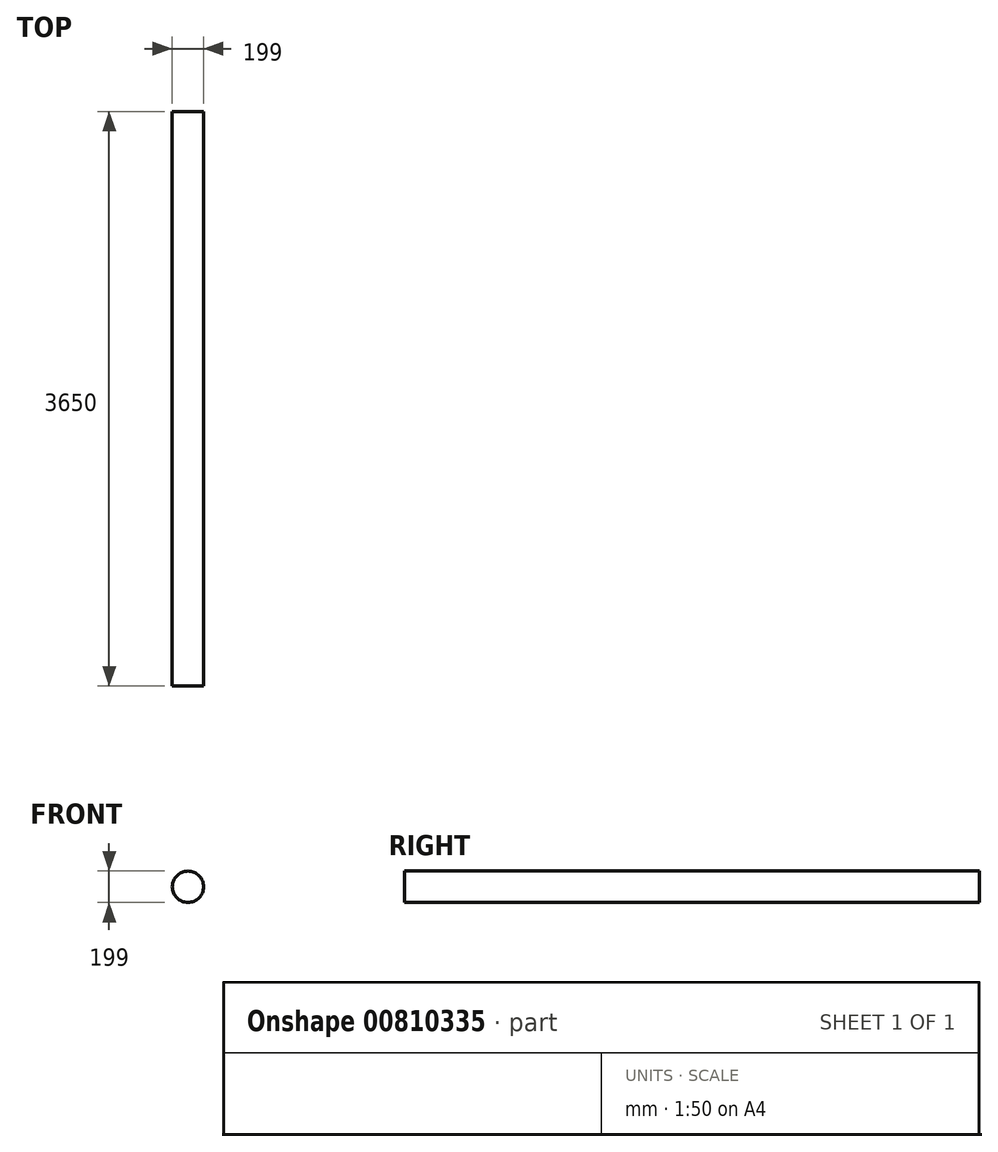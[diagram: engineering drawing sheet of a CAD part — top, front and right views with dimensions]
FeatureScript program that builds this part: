
annotation { "Feature Type Name" : "Feature", "Feature Type Description" : "" }
export const myFeature = defineFeature(function(context is Context, id is Id, definition is map)
    precondition{}
    {
        {
            var Q0;
            Q0=qCreatedBy(makeId("Front.planeOp"),FACE);
            var sketch = newSketch(context, id + "F0", { "sketchPlane" : qUnion([Q0])});
            skCircle(sketch, "E0", {"center": v(0, 0) * mm, "radius": 99.5 * mm});
            skSolve(sketch);
        }
        {
            var Q0;
            Q0 = qSketchRegion(id + "F0", true);
            extrude(context, id + "F1", {"entities" : qUnion([Q0]), "endBound" : BoundingType.SYMMETRIC, "depth" : 3650 * mm, "offsetDistance" : 25.4 * mm});
        }
    });
